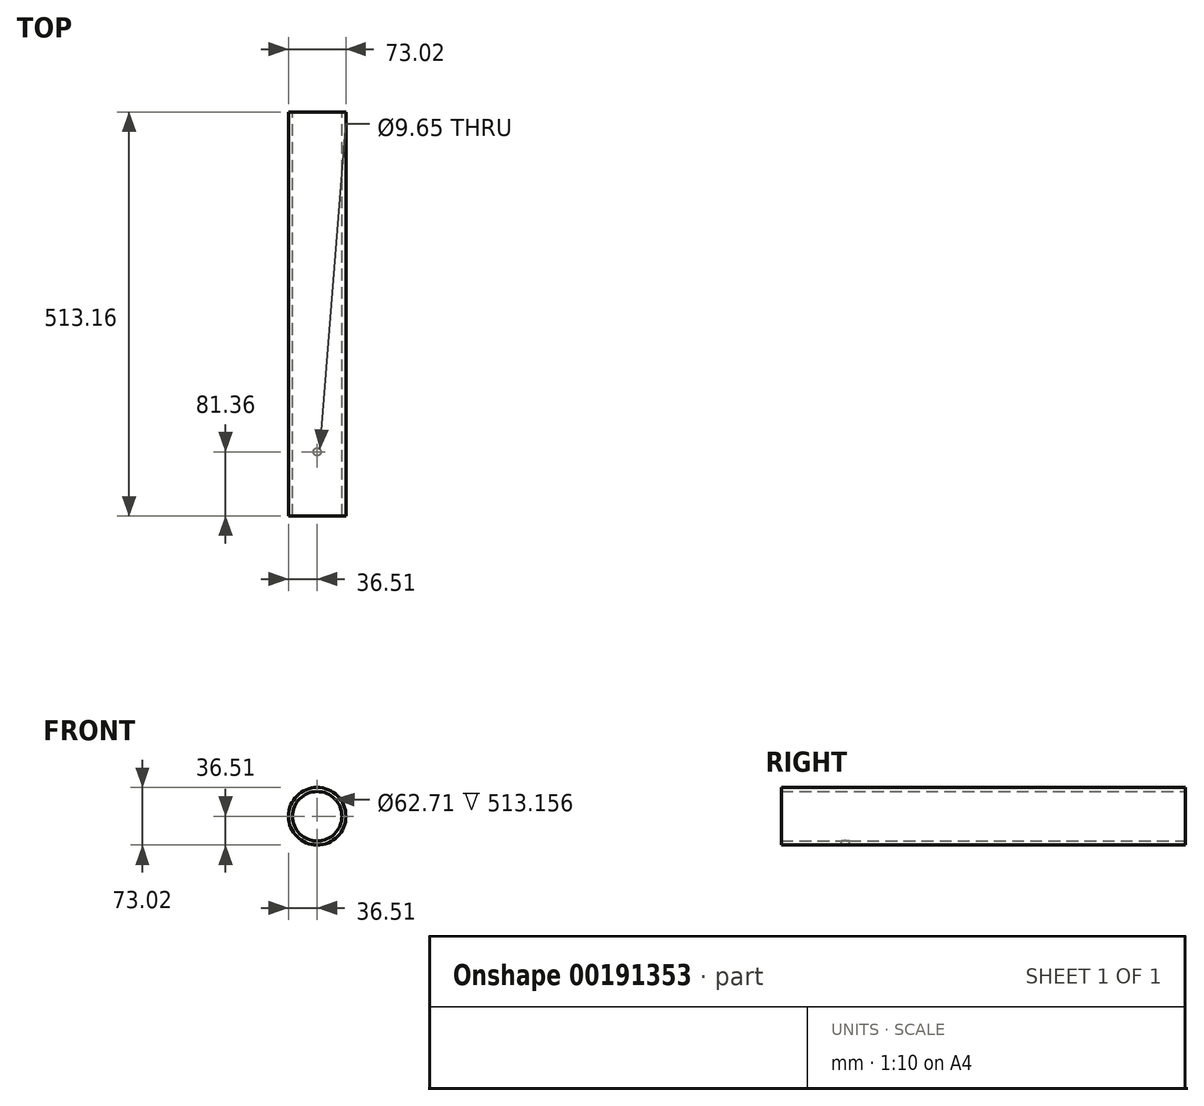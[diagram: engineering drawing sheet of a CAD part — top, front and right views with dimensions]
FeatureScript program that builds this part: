
annotation { "Feature Type Name" : "Feature", "Feature Type Description" : "" }
export const myFeature = defineFeature(function(context is Context, id is Id, definition is map)
    precondition{}
    {
        {
            var Q0;
            Q0=qCreatedBy(makeId("Front.planeOp"),FACE);
            var sketch = newSketch(context, id + "F0", { "sketchPlane" : qUnion([Q0])});
            skCircle(sketch, "E0", {"center": v(0, 0) * mm, "radius": 36.51 * mm});
            skCircle(sketch, "E1", {"center": v(0, 0) * mm, "radius": 31.36 * mm});
            skSolve(sketch);
        }
        {
            var Q0;
            Q0=makeQuery(id+"F0.imprint","IMPRINT",FACE,{"disambiguationData":[TD([[makeQuery(id+"F0.imprint","IMPRINT",EDGE,{"derivedFrom":sQuery(id+"F0.wireOp",EDGE,"E0")}),1.0]])]});
            extrude(context, id + "F1", {"entities" : qUnion([Q0]), "depth" : 5.16 * mm, "hasSecondDirection" : true, "secondDirectionOppositeDirection" : true, "secondDirectionDepth" : 508 * mm});
        }
        {
            var Q0;
            Q0=qCreatedBy(makeId("Top.planeOp"),FACE);
            var sketch = newSketch(context, id + "F2", { "sketchPlane" : qUnion([Q0])});
            skCircle(sketch, "E2", {"center": v(0, 76.2) * mm, "radius": 4.83 * mm});
            skLineSegment(sketch, "E3", {"start": v(0, 0) * mm, "end": v(0, 508) * mm, "construction": true});
            skSolve(sketch);
        }
        {
            var Q0;
            Q0=sQuery(id+"F2.wireOp",VERTEX,"E2.center");
            var Q1;
            Q1=makeQuery(id+"F1.opExtrude","SWEPT_BODY",BODY,{"disambiguationData":[OSD([sQuery(id+"F0.wireOp",EDGE,"E0"),sQuery(id+"F0.wireOp",EDGE,"E1")])]});
            hole(context, id + "F3", {"style" : HoleStyle.SIMPLE, "endStyle" : HoleEndStyle.BLIND, "holeDiameter" : 9.65 * mm, "holeDepth" : 6.35 * mm, "locations" : qUnion([Q0]), "scope" : qUnion([Q1])});
        }
    });
